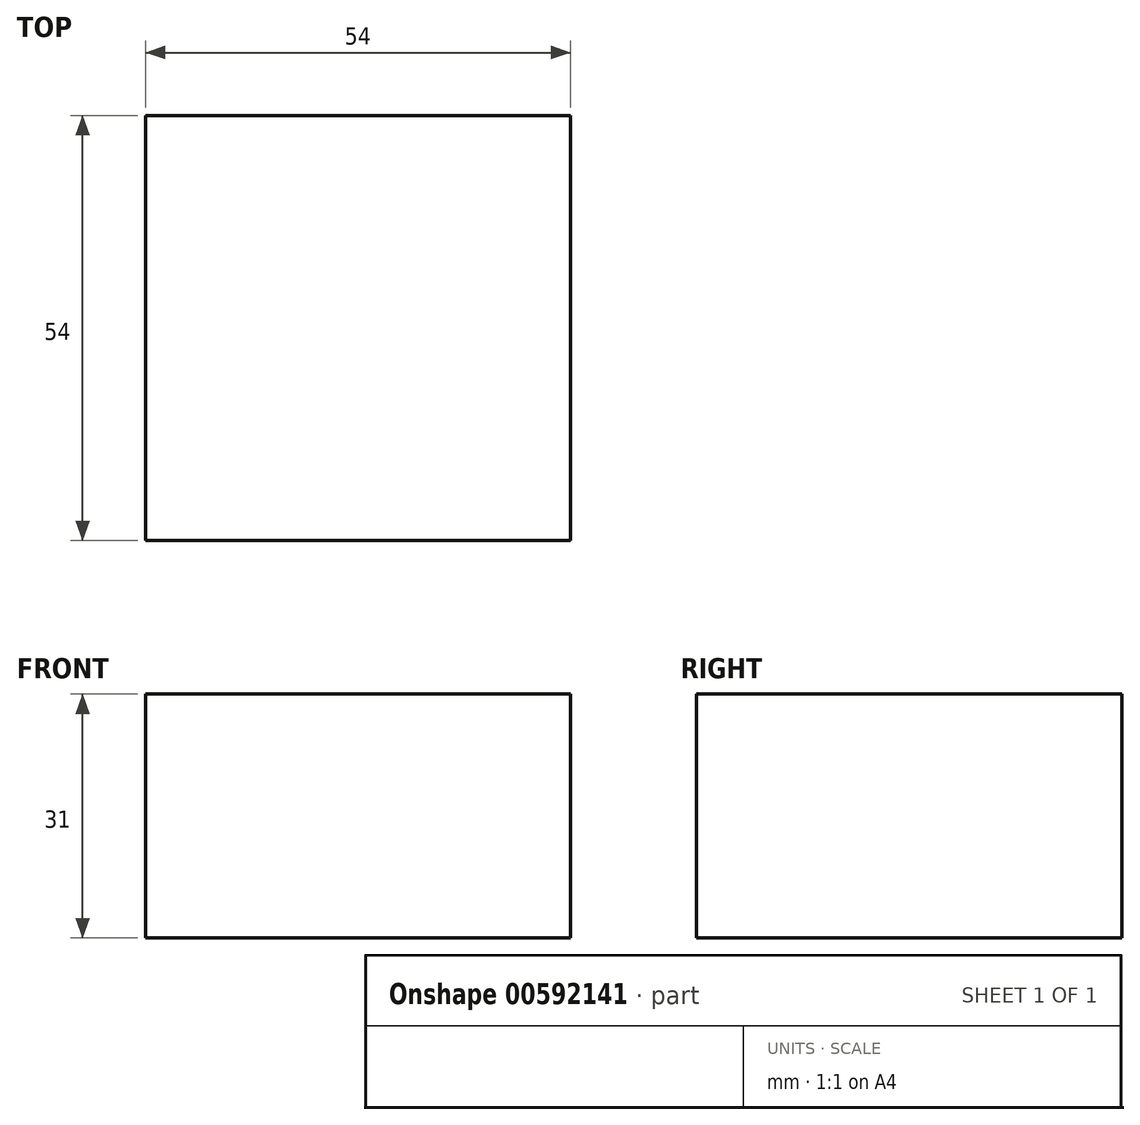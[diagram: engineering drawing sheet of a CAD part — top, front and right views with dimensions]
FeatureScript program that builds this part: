
annotation { "Feature Type Name" : "Feature", "Feature Type Description" : "" }
export const myFeature = defineFeature(function(context is Context, id is Id, definition is map)
    precondition{}
    {
        {
            var Q0;
            Q0=qCreatedBy(makeId("Top.planeOp"),FACE);
            var sketch = newSketch(context, id + "F0", { "sketchPlane" : qUnion([Q0])});
            skLineSegment(sketch, "E0.bottom", {"start": v(-64.23, 59.06) * mm, "end": v(-10.23, 59.06) * mm});
            skLineSegment(sketch, "E0.top", {"start": v(-64.23, 5.06) * mm, "end": v(-10.23, 5.06) * mm});
            skLineSegment(sketch, "E0.left", {"start": v(-64.23, 59.06) * mm, "end": v(-64.23, 5.06) * mm});
            skLineSegment(sketch, "E0.right", {"start": v(-10.23, 59.06) * mm, "end": v(-10.23, 5.06) * mm});
            skSolve(sketch);
        }
        {
            var Q0;
            Q0=makeQuery(id+"F0.imprint","IMPRINT",FACE,{"disambiguationData":[TD([[makeQuery(id+"F0.imprint","IMPRINT",EDGE,{"derivedFrom":sQuery(id+"F0.wireOp",EDGE,"E0.bottom")}),-1.0]])]});
            extrude(context, id + "F1", {"entities" : qUnion([Q0]), "depth" : 31 * mm, "offsetDistance" : 25 * mm});
        }
    });
